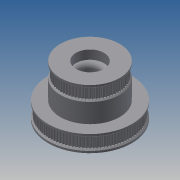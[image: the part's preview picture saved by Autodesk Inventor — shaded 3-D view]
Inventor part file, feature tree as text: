
AUTODESK INVENTOR PART (.ipt)
format: ipt  version: 2013 (Build 170138000, 138)  size: 1,186,304 bytes
history: native  units: mm
features: extrude x11, sketch x11, pattern_circular x2, chamfer x1, fillet x1
ambient origin geometry x8: Origin, YZ Plane, XZ Plane, XY Plane, X Axis, Y Axis, Z Axis, Center Point
bodies: Solid1 (feature_tree)
feature tree (26):
  extrude  "Extrusion1"  Depth=8.0mm TaperAngle=0.0deg
  extrude  "Extrusion2"  Depth=8.0mm TaperAngle=0.0deg
  pattern_circular  "Circular Pattern1"  Count=70 Angle=360.0deg
  extrude  "Extrusion3"  Depth=2.5mm TaperAngle=0.0deg
  extrude  "Extrusion4"  Depth=63.661977mm
  extrude  "Extrusion5"  Depth=1.59mm
  extrude  "Extrusion6"  Depth=1000.0mm TaperAngle=360.0deg
  pattern_circular  "Circular Pattern2"  [2 undecoded]
  extrude  "Extrusion7"  Depth=22.0mm
  extrude  "Extrusion8"  Depth=7.0mm TaperAngle=0.0deg
  chamfer  "Chamfer1"  Distance=7.0mm
  extrude  "Extrusion9"  Depth=3.5mm
  extrude  "Extrusion10"  [1 undecoded]
  extrude  "Extrusion11"  [1 undecoded]
  fillet  "Fillet1"  [1 undecoded]
  sketch  "Sketch1"  dims[d0=44.563384mm d2=8.0mm d3=0.0mm]
  sketch  "Sketch2"  dims[d4=1.59mm d6=8.0mm d7=0.0mm d8=700.0mm d9=360.0deg]
  sketch  "Sketch3"  dims[d11=1.0mm d12=2.5mm d13=0.0mm]
  sketch  "Sketch4"  dims[d14=16.1mm d15=0.0mm d16=63.661977mm]
  sketch  "Sketch5"  dims[d18=13.0mm d19=0.0mm d20=1.59mm]
  sketch  "Sketch6"  dims[d22=13.0mm d23=0.0mm d24=1000.0mm d25=360.0deg]
  sketch  "Sketch7"  dims[d27=1.0mm]
  sketch  "Sketch8"  dims[d28=2.5mm d29=0.0mm]
  sketch  "Sketch9"  dims[d30=2.5mm d31=0.0mm]
  sketch  "Sketch10"  dims[d32=1.0mm d33=2.0mm d34=45.0deg]
  sketch  "Sketch11"  dims[d35=15.0mm d37=2.5mm d38=0.0mm d39=22.0mm d41=7.0mm d42=0.0mm d43=7.0mm d44=0.0mm d45=3.5mm]
note: 5 required parameter values undecoded (feature->parameter linkage not recoverable at this tier; creation-order binding heuristic only, values carry confidence <= 0.55)
